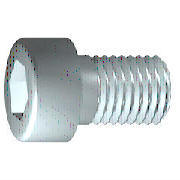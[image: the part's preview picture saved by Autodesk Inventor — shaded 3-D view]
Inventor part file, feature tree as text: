
AUTODESK INVENTOR PART (.ipt)
format: ipt  version: 2021 (Build 250183000, 183)  size: 193,536 bytes
history: native  units: mm (DEFAULTED — no unit token found)
features: sketch x2, extrude x1, plane x1, fillet x1
ambient origin geometry x7: Origin, YZ Plane, XY Plane, X Axis, Y Axis, Z Axis, Center Point
bodies: Solid1 (feature_tree), Body (feature_tree)
feature tree (5):
  extrude  "Slot"  Depth=8.0mm
  plane  "Work Plane1"
  fillet  "Fillet2"  Radius=8.0mm
  sketch  "Sketch1"  dims[d1=16.875mm d2=0.766912mm d3=8.0mm]
  sketch  "Sketch2"  dims[d4=4.0mm d5=60.0deg d6=8.0mm d7=8.0mm d8=6.928203mm d9=13.0mm d10=90.0deg d11=10.0mm d12=0.0mm d13=16.875mm d14=0.0mm d15=0.766813mm d16=0.766813mm d17=0.8mm d19=0.0mm d26=20.0mm d27=45.0deg d28=0.0mm d29=0.0mm d30=0.1mm]
